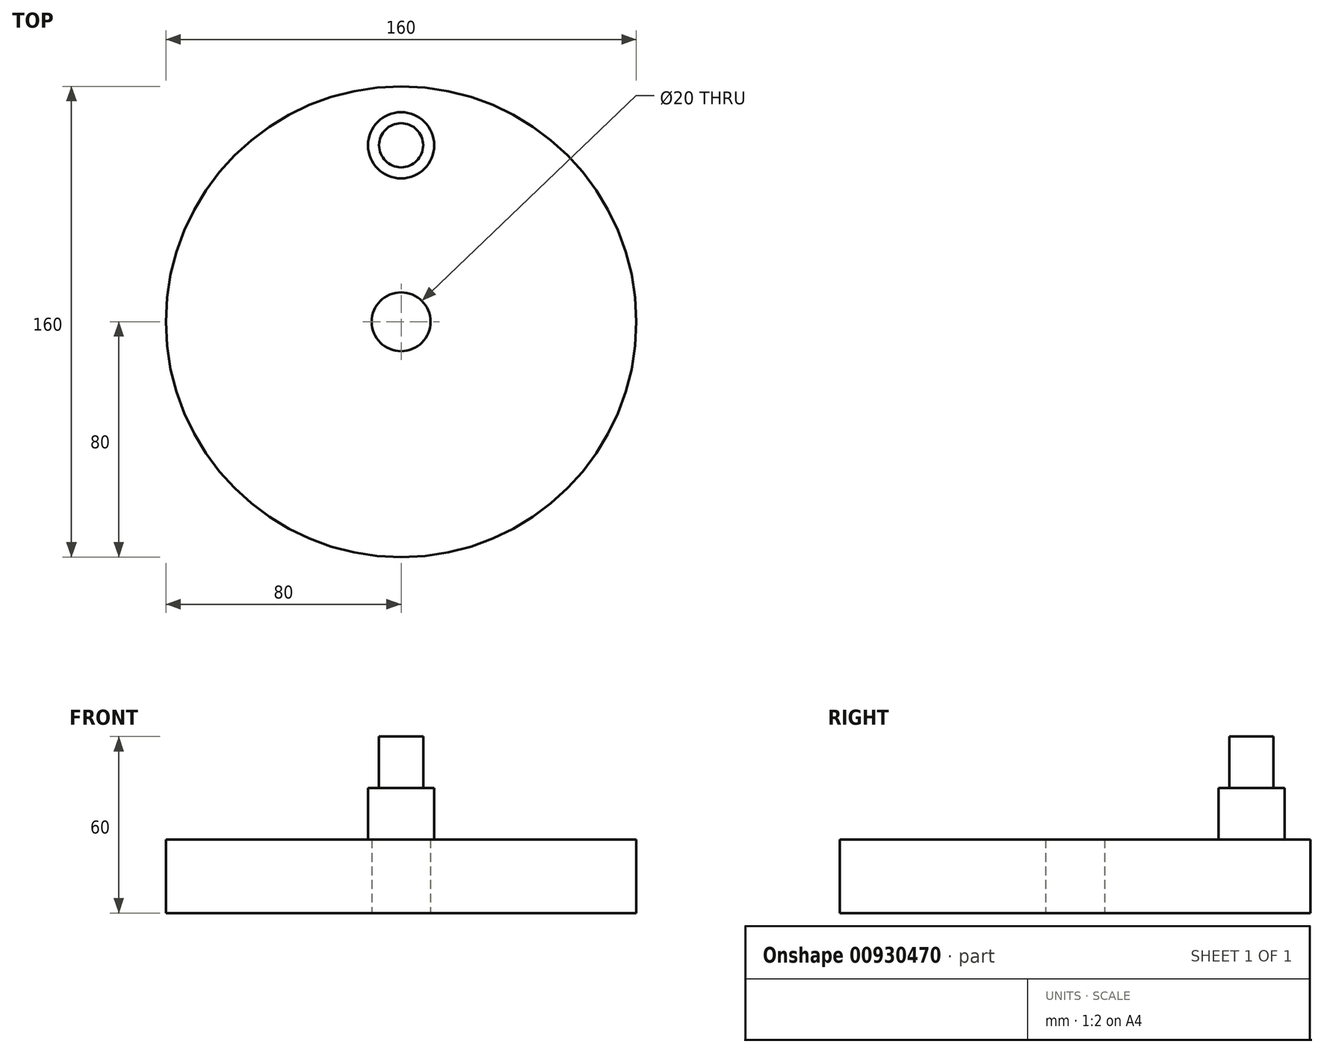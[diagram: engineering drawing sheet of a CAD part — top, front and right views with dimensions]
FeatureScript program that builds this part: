
annotation { "Feature Type Name" : "Feature", "Feature Type Description" : "" }
export const myFeature = defineFeature(function(context is Context, id is Id, definition is map)
    precondition{}
    {
        {
            var Q0;
            Q0=qCreatedBy(makeId("Top.planeOp"),FACE);
            var sketch = newSketch(context, id + "F0", { "sketchPlane" : qUnion([Q0])});
            skCircle(sketch, "E0", {"center": v(0, 0) * mm, "radius": 80 * mm});
            skCircle(sketch, "E1", {"center": v(0, 0) * mm, "radius": 10 * mm});
            skSolve(sketch);
        }
        {
            var Q0;
            Q0=makeQuery(id+"F0.imprint","IMPRINT",FACE,{"disambiguationData":[TD([[makeQuery(id+"F0.imprint","IMPRINT",EDGE,{"derivedFrom":sQuery(id+"F0.wireOp",EDGE,"E0")}),1.0]])]});
            extrude(context, id + "F1", {"entities" : qUnion([Q0]), "depth" : 25 * mm, "offsetDistance" : 25 * mm});
        }
        {
            var Q0;
            Q0=makeQuery(id+"F1.opExtrude","CAP_FACE",FACE,{"disambiguationData":[OSD([sQuery(id+"F0.wireOp",EDGE,"E0"),sQuery(id+"F0.wireOp",EDGE,"E1")])],"isStart":false});
            var sketch = newSketch(context, id + "F2", { "sketchPlane" : qUnion([Q0])});
            skPoint(sketch, "E2.orphan", {"position": v(0, 0) * mm});
            skCircle(sketch, "E3", {"center": v(0, 60) * mm, "radius": 7.5 * mm});
            skSolve(sketch);
        }
        {
            var Q0;
            Q0=makeQuery(id+"F2.imprint","IMPRINT",FACE,{"disambiguationData":[TD([[makeQuery(id+"F2.imprint","IMPRINT",EDGE,{"derivedFrom":sQuery(id+"F2.wireOp",EDGE,"E3")}),1.0]])]});
            extrude(context, id + "F3", {"entities" : qUnion([Q0]), "operationType" : NewBodyOperationType.ADD, "depth" : 35 * mm, "offsetDistance" : 25 * mm});
        }
        {
            var Q0;
            Q0=makeQuery(id+"F1.opExtrude","CAP_FACE",FACE,{"disambiguationData":[OSD([sQuery(id+"F0.wireOp",EDGE,"E0"),sQuery(id+"F0.wireOp",EDGE,"E1")])],"isStart":false});
            var sketch = newSketch(context, id + "F4", { "sketchPlane" : qUnion([Q0])});
            skCircle(sketch, "E4", {"center": v(0, 60) * mm, "radius": 11.25 * mm});
            skSolve(sketch);
        }
        {
            var Q0;
            Q0=makeQuery(id+"F4.imprint","IMPRINT",FACE,{"disambiguationData":[TD([[makeQuery(id+"F4.imprint","IMPRINT",EDGE,{"derivedFrom":makeQuery(id+"F3.opExtrude","CAP_EDGE",EDGE,{"disambiguationData":[OSD([sQuery(id+"F2.wireOp",EDGE,"E3")])],"isStart":true})}),1.0]])]});
            var Q1;
            Q1=makeQuery(id+"F4.imprint","IMPRINT",FACE,{"disambiguationData":[TD([[makeQuery(id+"F4.imprint","IMPRINT",EDGE,{"derivedFrom":sQuery(id+"F4.wireOp",EDGE,"E4")}),1.0]])]});
            extrude(context, id + "F5", {"entities" : qUnion([Q0, Q1]), "operationType" : NewBodyOperationType.ADD, "depth" : 17.5 * mm, "offsetDistance" : 25 * mm});
        }
    });
